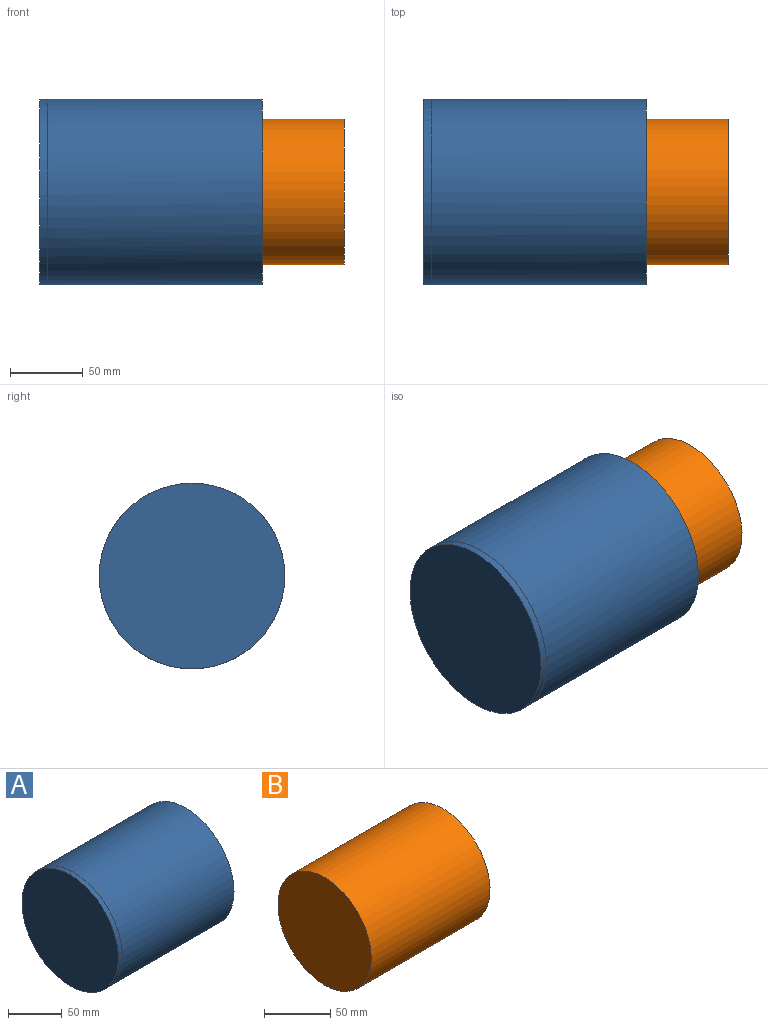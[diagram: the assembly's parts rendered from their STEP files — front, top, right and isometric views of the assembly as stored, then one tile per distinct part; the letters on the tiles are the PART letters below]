
ASSEMBLY  parts=2 mates=1
PART A: 7 faces, bbox 152.4x127.1x127.1 mm
  f0: cylinder r=50.8mm len=147.32mm, axis (-1,0,0), area 47022.5mm2, adj f2,f6
  f1: cylinder r=63.5mm len=147.32mm, axis (-1,0,0), area 58778.1mm2, adj f2,f3
  f2: plane 127x127mm, normal (1,0,0), area 4560.4mm2, adj f0,f1
  f3: plane 127.05x127.05mm, normal (1,0,0), area 10.2mm2, adj f1,f4
  f4: cylinder r=63.53mm len=127.05mm, axis (-1,0,0), area 2027.6mm2, adj f3,f5
  f5: plane 127.05x127.05mm, normal (-1,0,0), area 12677.9mm2, adj f4
  f6: plane 101.6x101.6mm, normal (1,0,0), area 8107.3mm2, adj f0
PART B: 3 faces, bbox 127x99.8x99.8 mm
  f0: cylinder r=49.89mm len=127mm, axis (-1,0,0), area 39810.4mm2, adj f1,f2
  f1: plane 99.78x99.78mm, normal (1,0,0), area 7819.4mm2, adj f0
  f2: plane 99.78x99.78mm, normal (-1,0,0), area 7819.4mm2, adj f0
PLACE A t=(-42.8,19.42,6.8)mm fixed
PLACE B t=(33.4,19.42,6.8)mm
MATE slider A.f1 <-> B.f0  axis (-1,0,0) through (-37.72,19.42,6.8)mm
